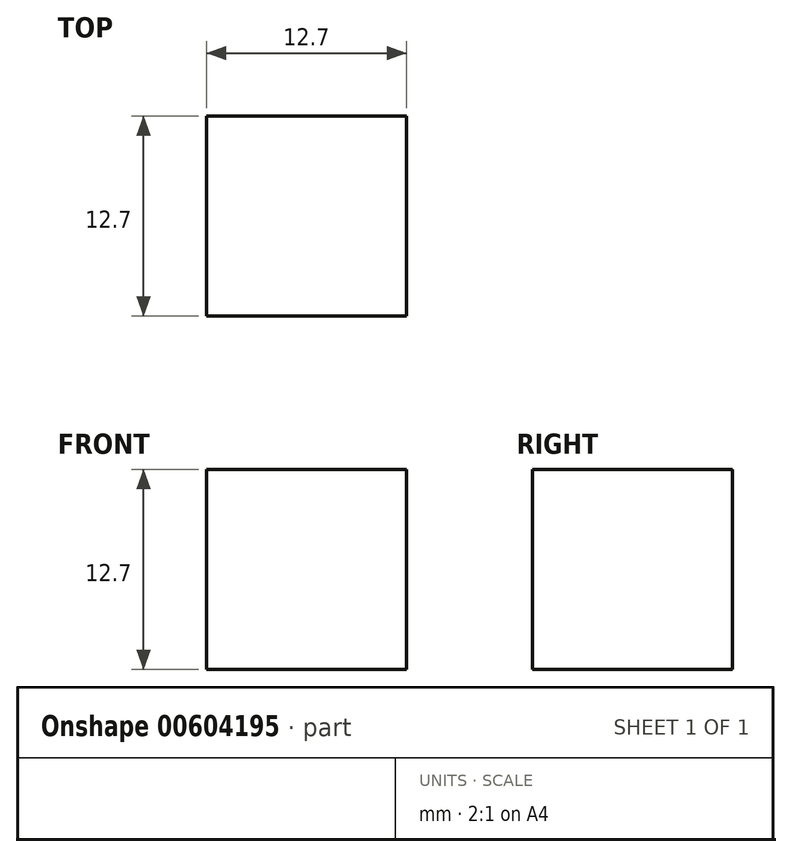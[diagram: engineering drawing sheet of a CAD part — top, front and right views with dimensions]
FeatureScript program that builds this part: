
annotation { "Feature Type Name" : "Feature", "Feature Type Description" : "" }
export const myFeature = defineFeature(function(context is Context, id is Id, definition is map)
    precondition{}
    {
        {
            var Q0;
            Q0=qCreatedBy(makeId("Top.planeOp"),FACE);
            var sketch = newSketch(context, id + "F0", { "sketchPlane" : qUnion([Q0])});
            skLineSegment(sketch, "E0.bottom", {"start": v(6.35, 6.35) * mm, "end": v(-6.35, 6.35) * mm});
            skLineSegment(sketch, "E0.top", {"start": v(6.35, -6.35) * mm, "end": v(-6.35, -6.35) * mm});
            skLineSegment(sketch, "E0.left", {"start": v(6.35, 6.35) * mm, "end": v(6.35, -6.35) * mm});
            skLineSegment(sketch, "E0.right", {"start": v(-6.35, 6.35) * mm, "end": v(-6.35, -6.35) * mm});
            skPoint(sketch, "E0.middle", {"position": v(0, 0) * mm});
            skSolve(sketch);
        }
        {
            var Q0;
            Q0 = qSketchRegion(id + "F0", true);
            extrude(context, id + "F1", {"entities" : qUnion([Q0]), "depth" : 12.7 * mm, "offsetDistance" : 25.4 * mm});
        }
    });
